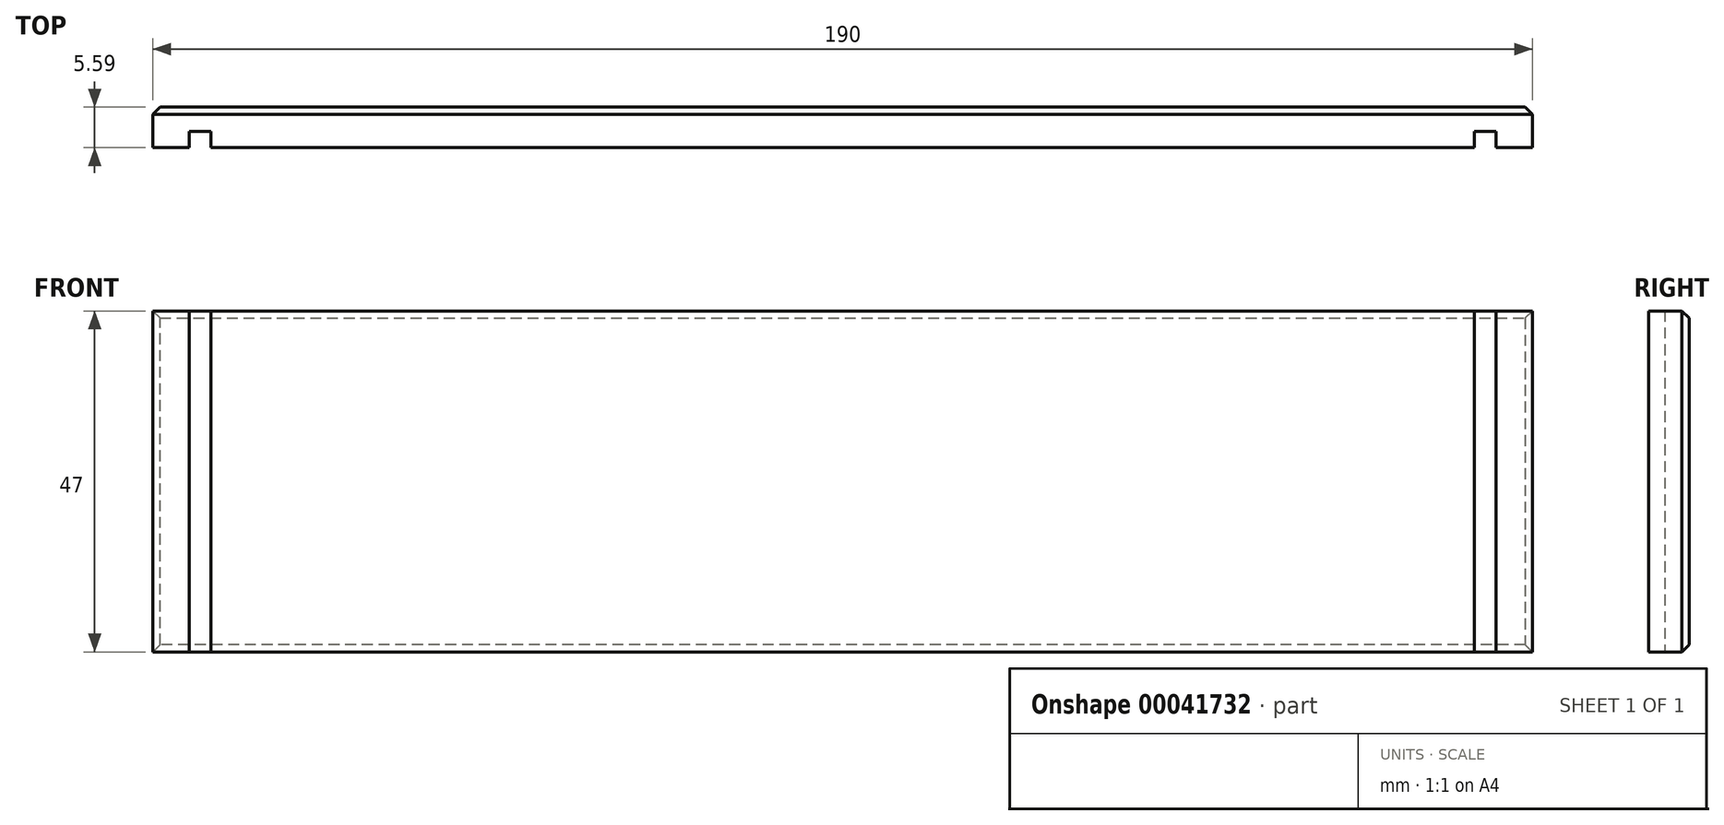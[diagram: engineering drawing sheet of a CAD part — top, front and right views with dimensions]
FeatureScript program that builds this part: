
annotation { "Feature Type Name" : "Feature", "Feature Type Description" : "" }
export const myFeature = defineFeature(function(context is Context, id is Id, definition is map)
    precondition{}
    {
        {
            var Q0;
            Q0=qCreatedBy(makeId("Top.planeOp"),FACE);
            var sketch = newSketch(context, id + "F0", { "sketchPlane" : qUnion([Q0])});
            skLineSegment(sketch, "E0", {"start": v(0, 0) * mm, "end": v(-95, 0) * mm});
            skLineSegment(sketch, "E1", {"start": v(0, 0) * mm, "end": v(0, -5.59) * mm});
            skLineSegment(sketch, "E2", {"start": v(0, -5.59) * mm, "end": v(-5, -5.59) * mm});
            skLineSegment(sketch, "E3", {"start": v(-5, -5.59) * mm, "end": v(-5, -3.35) * mm});
            skLineSegment(sketch, "E4", {"start": v(-5, -3.35) * mm, "end": v(-8, -3.35) * mm});
            skLineSegment(sketch, "E5", {"start": v(-8, -3.35) * mm, "end": v(-8, -5.59) * mm});
            skLineSegment(sketch, "E6", {"start": v(-8, -5.59) * mm, "end": v(-95, -5.59) * mm});
            skLineSegment(sketch, "E7", {"start": v(-95, 0) * mm, "end": v(-95, -5.59) * mm});
            skLineSegment(sketch, "E8.MirrorCS", {"start": v(-190, 0) * mm, "end": v(-95, 0) * mm});
            skLineSegment(sketch, "E9.MirrorCS", {"start": v(-182, -5.59) * mm, "end": v(-95, -5.59) * mm});
            skLineSegment(sketch, "E10.MirrorCS", {"start": v(-190, 0) * mm, "end": v(-190, -5.59) * mm});
            skLineSegment(sketch, "E11.MirrorCS", {"start": v(-190, -5.59) * mm, "end": v(-185, -5.59) * mm});
            skLineSegment(sketch, "E12.MirrorCS", {"start": v(-185, -5.59) * mm, "end": v(-185, -3.35) * mm});
            skLineSegment(sketch, "E13.MirrorCS", {"start": v(-185, -3.35) * mm, "end": v(-182, -3.35) * mm});
            skLineSegment(sketch, "E14.MirrorCS", {"start": v(-182, -3.35) * mm, "end": v(-182, -5.59) * mm});
            skSolve(sketch);
        }
        {
            var Q0;
            Q0=qSketchRegion(id+"F0",true);
            extrude(context, id + "F1", {"entities" : qUnion([Q0]), "depth" : 47 * mm});
        }
        {
            var Q0;
            Q0=makeQuery(id+"F1.opExtrude","SWEPT_FACE",FACE,{"disambiguationData":[OSD([sQuery(id+"F0.wireOp",EDGE,"E0"),sQuery(id+"F0.wireOp",EDGE,"E8.MirrorCS")])]});
            chamfer(context, id + "F2", {"entities" : qUnion([Q0]), "width" : 1 * mm, "tangentPropagation" : true});
        }
    });
